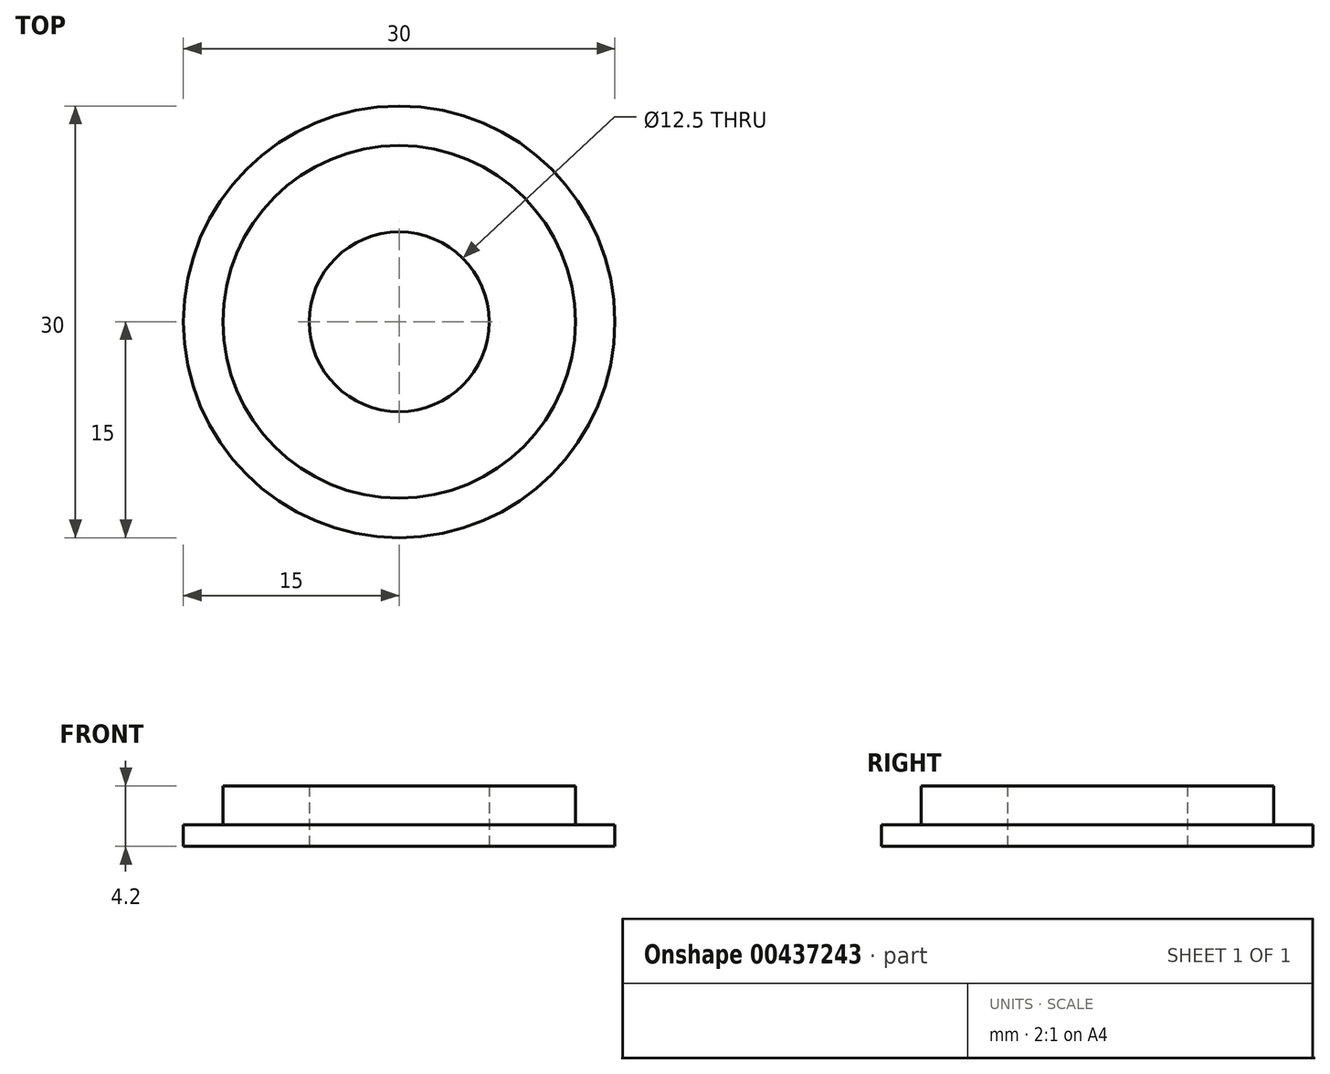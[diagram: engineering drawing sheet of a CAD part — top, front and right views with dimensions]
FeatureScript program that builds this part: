
annotation { "Feature Type Name" : "Feature", "Feature Type Description" : "" }
export const myFeature = defineFeature(function(context is Context, id is Id, definition is map)
    precondition{}
    {
        {
            var Q0;
            Q0=qCreatedBy(makeId("Top.planeOp"),FACE);
            var sketch = newSketch(context, id + "F0", { "sketchPlane" : qUnion([Q0])});
            skCircle(sketch, "E0", {"center": v(0, 0) * mm, "radius": 12.25 * mm});
            skSolve(sketch);
        }
        {
            var Q0;
            Q0 = qSketchRegion(id + "F0", true);
            extrude(context, id + "F1", {"entities" : qUnion([Q0]), "depth" : 2.7 * mm});
        }
        {
            var Q0;
            Q0=makeQuery(id+"F1.opExtrude","CAP_FACE",FACE,{"disambiguationData":[OSD([sQuery(id+"F0.wireOp",EDGE,"E0")])],"isStart":true});
            var sketch = newSketch(context, id + "F2", { "sketchPlane" : qUnion([Q0])});
            skCircle(sketch, "E1", {"center": v(0, 0) * mm, "radius": 15 * mm});
            skSolve(sketch);
        }
        {
            var Q0;
            Q0=makeQuery(id+"F2.imprint","IMPRINT",FACE,{"disambiguationData":[TD([[makeQuery(id+"F2.imprint","IMPRINT",EDGE,{"derivedFrom":sQuery(id+"F2.wireOp",EDGE,"E1")}),1.0]])]});
            var Q1;
            Q1=makeQuery(id+"F2.imprint","IMPRINT",FACE,{"disambiguationData":[TD([[makeQuery(id+"F2.imprint","IMPRINT",EDGE,{"derivedFrom":makeQuery(id+"F1.opExtrude","CAP_EDGE",EDGE,{"disambiguationData":[OSD([sQuery(id+"F0.wireOp",EDGE,"E0")])],"isStart":true})}),-1.0]])]});
            extrude(context, id + "F3", {"entities" : qUnion([Q0, Q1]), "operationType" : NewBodyOperationType.ADD, "depth" : 1.5 * mm});
        }
        {
            var Q0;
            Q0=makeQuery(id+"F3.opExtrude","CAP_FACE",FACE,{"disambiguationData":[OSD([sQuery(id+"F2.wireOp",EDGE,"E1")])],"isStart":false});
            var sketch = newSketch(context, id + "F4", { "sketchPlane" : qUnion([Q0])});
            skCircle(sketch, "E2", {"center": v(0, 0) * mm, "radius": 6.25 * mm});
            skSolve(sketch);
        }
        {
            var Q0;
            Q0=makeQuery(id+"F4.imprint","IMPRINT",FACE,{"disambiguationData":[TD([[makeQuery(id+"F4.imprint","IMPRINT",EDGE,{"derivedFrom":sQuery(id+"F4.wireOp",EDGE,"E2")}),1.0]])]});
            extrude(context, id + "F5", {"entities" : qUnion([Q0]), "operationType" : NewBodyOperationType.REMOVE, "oppositeDirection" : true, "depth" : 10 * mm});
        }
    });
